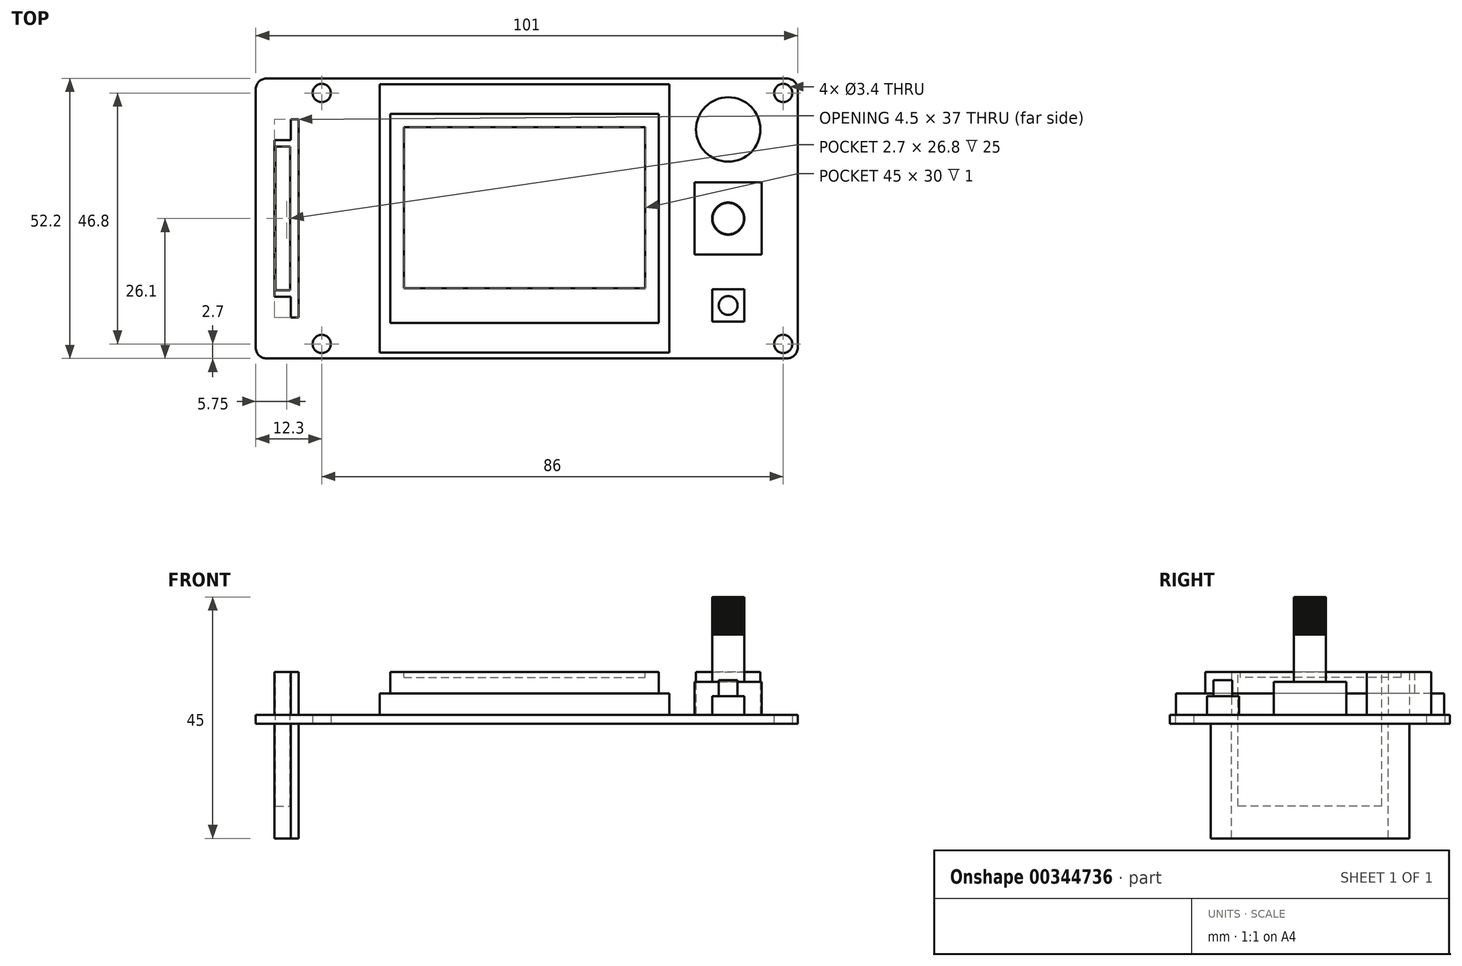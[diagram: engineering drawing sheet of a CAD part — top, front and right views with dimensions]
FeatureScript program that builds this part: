
annotation { "Feature Type Name" : "Feature", "Feature Type Description" : "" }
export const myFeature = defineFeature(function(context is Context, id is Id, definition is map)
    precondition{}
    {
        {
            var Q0;
            Q0=qCreatedBy(makeId("Top.planeOp"),FACE);
            var sketch = newSketch(context, id + "F0", { "sketchPlane" : qUnion([Q0])});
            skLineSegment(sketch, "E0.bottom", {"start": v(2, 0) * mm, "end": v(99, 0) * mm});
            skLineSegment(sketch, "E0.top", {"start": v(2, 52.2) * mm, "end": v(99, 52.2) * mm});
            skLineSegment(sketch, "E0.left", {"start": v(0, 2) * mm, "end": v(0, 50.2) * mm});
            skLineSegment(sketch, "E0.right", {"start": v(101, 2) * mm, "end": v(101, 50.2) * mm});
            skPoint(sketch, "E1.visualSharp", {"position": v(0, 52.2) * mm});
            skArc(sketch, "E1.filletArc", {"start": v(2, 52.2) * mm, "mid": v(0.59, 51.61) * mm, "end": v(0, 50.2) * mm});
            skPoint(sketch, "E2.visualSharp", {"position": v(101, 52.2) * mm});
            skArc(sketch, "E2.filletArc", {"start": v(101, 50.2) * mm, "mid": v(100.41, 51.61) * mm, "end": v(99, 52.2) * mm});
            skPoint(sketch, "E3.visualSharp", {"position": v(101, 0) * mm});
            skArc(sketch, "E3.filletArc", {"start": v(99, 0) * mm, "mid": v(100.41, 0.59) * mm, "end": v(101, 2) * mm});
            skPoint(sketch, "E4.visualSharp", {"position": v(0, 0) * mm});
            skArc(sketch, "E4.filletArc", {"start": v(0, 2) * mm, "mid": v(0.59, 0.59) * mm, "end": v(2, 0) * mm});
            skCircle(sketch, "E5", {"center": v(12.3, 49.5) * mm, "radius": 1.7 * mm});
            skCircle(sketch, "E6", {"center": v(98.3, 49.5) * mm, "radius": 1.7 * mm});
            skCircle(sketch, "E7", {"center": v(98.3, 2.7) * mm, "radius": 1.7 * mm});
            skCircle(sketch, "E8", {"center": v(12.3, 2.7) * mm, "radius": 1.7 * mm});
            skLineSegment(sketch, "E9", {"start": v(12.3, 49.5) * mm, "end": v(98.3, 49.5) * mm, "construction": true});
            skLineSegment(sketch, "E10", {"start": v(98.3, 2.7) * mm, "end": v(98.3, 49.5) * mm, "construction": true});
            skLineSegment(sketch, "E11", {"start": v(12.3, 2.7) * mm, "end": v(12.3, 49.5) * mm, "construction": true});
            skLineSegment(sketch, "E12", {"start": v(12.3, 2.7) * mm, "end": v(98.3, 2.7) * mm, "construction": true});
            skLineSegment(sketch, "E13", {"start": v(0, 26.1) * mm, "end": v(12.3, 26.1) * mm, "construction": true});
            skLineSegment(sketch, "E14", {"start": v(98.3, 26.1) * mm, "end": v(101, 26.1) * mm, "construction": true});
            skSolve(sketch);
        }
        {
            var Q0;
            Q0 = qSketchRegion(id + "F0", true);
            extrude(context, id + "F1", {"entities" : qUnion([Q0]), "depth" : 1.6 * mm});
        }
        {
            var Q0;
            Q0=makeQuery(id+"F1.opExtrude","CAP_FACE",FACE,{"disambiguationData":[OSD([sQuery(id+"F0.wireOp",EDGE,"E0.bottom"),sQuery(id+"F0.wireOp",EDGE,"E0.top"),sQuery(id+"F0.wireOp",EDGE,"E0.left"),sQuery(id+"F0.wireOp",EDGE,"E0.right"),sQuery(id+"F0.wireOp",EDGE,"E1.filletArc"),sQuery(id+"F0.wireOp",EDGE,"E2.filletArc"),sQuery(id+"F0.wireOp",EDGE,"E3.filletArc"),sQuery(id+"F0.wireOp",EDGE,"E4.filletArc"),sQuery(id+"F0.wireOp",EDGE,"E5"),sQuery(id+"F0.wireOp",EDGE,"E6"),sQuery(id+"F0.wireOp",EDGE,"E7"),sQuery(id+"F0.wireOp",EDGE,"E8")])],"isStart":false});
            var sketch = newSketch(context, id + "F2", { "sketchPlane" : qUnion([Q0])});
            skLineSegment(sketch, "E15.bottom", {"start": v(23.1, 51.1) * mm, "end": v(77.1, 51.1) * mm});
            skLineSegment(sketch, "E15.top", {"start": v(23.1, 1.1) * mm, "end": v(77.1, 1.1) * mm});
            skLineSegment(sketch, "E15.left", {"start": v(23.1, 51.1) * mm, "end": v(23.1, 1.1) * mm});
            skLineSegment(sketch, "E15.right", {"start": v(77.1, 51.1) * mm, "end": v(77.1, 1.1) * mm});
            skSolve(sketch);
        }
        {
            var Q0;
            Q0 = qSketchRegion(id + "F2", true);
            extrude(context, id + "F3", {"entities" : qUnion([Q0]), "operationType" : NewBodyOperationType.ADD, "depth" : 4 * mm});
        }
        {
            var Q0;
            Q0=makeQuery(id+"F3.opExtrude","CAP_FACE",FACE,{"disambiguationData":[OSD([sQuery(id+"F2.wireOp",EDGE,"E15.bottom"),sQuery(id+"F2.wireOp",EDGE,"E15.top"),sQuery(id+"F2.wireOp",EDGE,"E15.left"),sQuery(id+"F2.wireOp",EDGE,"E15.right")])],"isStart":false});
            var sketch = newSketch(context, id + "F4", { "sketchPlane" : qUnion([Q0])});
            skLineSegment(sketch, "E16", {"start": v(25.1, 45.6) * mm, "end": v(75.1, 45.6) * mm});
            skLineSegment(sketch, "E17", {"start": v(50.1, 51.1) * mm, "end": v(50.1, 45.6) * mm, "construction": true});
            skLineSegment(sketch, "E18", {"start": v(25.1, 45.6) * mm, "end": v(25.1, 6.6) * mm});
            skLineSegment(sketch, "E19", {"start": v(25.1, 6.6) * mm, "end": v(75.1, 6.6) * mm});
            skLineSegment(sketch, "E20", {"start": v(75.1, 6.6) * mm, "end": v(75.1, 45.6) * mm});
            skSolve(sketch);
        }
        {
            var Q0;
            Q0 = qSketchRegion(id + "F4", true);
            extrude(context, id + "F5", {"entities" : qUnion([Q0]), "operationType" : NewBodyOperationType.ADD, "depth" : 4 * mm});
        }
        {
            var Q0;
            Q0=makeQuery(id+"F1.opExtrude","CAP_FACE",FACE,{"disambiguationData":[OSD([sQuery(id+"F0.wireOp",EDGE,"E0.bottom"),sQuery(id+"F0.wireOp",EDGE,"E0.top"),sQuery(id+"F0.wireOp",EDGE,"E0.left"),sQuery(id+"F0.wireOp",EDGE,"E0.right"),sQuery(id+"F0.wireOp",EDGE,"E1.filletArc"),sQuery(id+"F0.wireOp",EDGE,"E2.filletArc"),sQuery(id+"F0.wireOp",EDGE,"E3.filletArc"),sQuery(id+"F0.wireOp",EDGE,"E4.filletArc"),sQuery(id+"F0.wireOp",EDGE,"E5"),sQuery(id+"F0.wireOp",EDGE,"E6"),sQuery(id+"F0.wireOp",EDGE,"E7"),sQuery(id+"F0.wireOp",EDGE,"E8")])],"isStart":false});
            var sketch = newSketch(context, id + "F6", { "sketchPlane" : qUnion([Q0])});
            skLineSegment(sketch, "E21", {"start": v(8, 44.6) * mm, "end": v(8, 7.6) * mm});
            skLineSegment(sketch, "E22", {"start": v(8, 7.6) * mm, "end": v(6.5, 7.6) * mm});
            skLineSegment(sketch, "E23", {"start": v(6.5, 7.6) * mm, "end": v(6.5, 11.5) * mm});
            skLineSegment(sketch, "E24", {"start": v(6.5, 11.5) * mm, "end": v(3.5, 11.5) * mm});
            skLineSegment(sketch, "E25", {"start": v(3.5, 11.5) * mm, "end": v(3.5, 40.7) * mm});
            skLineSegment(sketch, "E26", {"start": v(3.5, 40.7) * mm, "end": v(6.5, 40.7) * mm});
            skLineSegment(sketch, "E27", {"start": v(6.5, 40.7) * mm, "end": v(6.5, 44.6) * mm});
            skLineSegment(sketch, "E28", {"start": v(6.5, 44.6) * mm, "end": v(8, 44.6) * mm});
            skLineSegment(sketch, "E29", {"start": v(3.5, 26.1) * mm, "end": v(8, 26.1) * mm, "construction": true});
            skSolve(sketch);
        }
        {
            var Q0;
            Q0 = qSketchRegion(id + "F6", true);
            extrude(context, id + "F7", {"entities" : qUnion([Q0]), "operationType" : NewBodyOperationType.ADD, "depth" : 8 * mm});
        }
        {
            var Q0;
            Q0 = qSketchRegion(id + "F6", true);
            extrude(context, id + "F8", {"entities" : qUnion([Q0]), "operationType" : NewBodyOperationType.ADD, "oppositeDirection" : true, "depth" : 23 * mm});
        }
        {
            var Q0;
            Q0=makeQuery(id+"F7.opExtrude","CAP_FACE",FACE,{"disambiguationData":[OSD([sQuery(id+"F6.wireOp",EDGE,"E21"),sQuery(id+"F6.wireOp",EDGE,"E22"),sQuery(id+"F6.wireOp",EDGE,"E23"),sQuery(id+"F6.wireOp",EDGE,"E24"),sQuery(id+"F6.wireOp",EDGE,"E25"),sQuery(id+"F6.wireOp",EDGE,"E26"),sQuery(id+"F6.wireOp",EDGE,"E27"),sQuery(id+"F6.wireOp",EDGE,"E28")])],"isStart":false});
            var sketch = newSketch(context, id + "F9", { "sketchPlane" : qUnion([Q0])});
            skLineSegment(sketch, "E30.bottom", {"start": v(3.7, 39.5) * mm, "end": v(6.4, 39.5) * mm});
            skLineSegment(sketch, "E30.top", {"start": v(3.7, 12.7) * mm, "end": v(6.4, 12.7) * mm});
            skLineSegment(sketch, "E30.left", {"start": v(3.7, 39.5) * mm, "end": v(3.7, 12.7) * mm});
            skLineSegment(sketch, "E30.right", {"start": v(6.4, 39.5) * mm, "end": v(6.4, 12.7) * mm});
            skSolve(sketch);
        }
        {
            var Q0;
            Q0 = qSketchRegion(id + "F9", true);
            extrude(context, id + "F10", {"entities" : qUnion([Q0]), "operationType" : NewBodyOperationType.REMOVE, "oppositeDirection" : true, "depth" : 25 * mm});
        }
        {
            var Q0;
            Q0=makeQuery(id+"F1.opExtrude","CAP_FACE",FACE,{"disambiguationData":[OSD([sQuery(id+"F0.wireOp",EDGE,"E0.bottom"),sQuery(id+"F0.wireOp",EDGE,"E0.top"),sQuery(id+"F0.wireOp",EDGE,"E0.left"),sQuery(id+"F0.wireOp",EDGE,"E0.right"),sQuery(id+"F0.wireOp",EDGE,"E1.filletArc"),sQuery(id+"F0.wireOp",EDGE,"E2.filletArc"),sQuery(id+"F0.wireOp",EDGE,"E3.filletArc"),sQuery(id+"F0.wireOp",EDGE,"E4.filletArc"),sQuery(id+"F0.wireOp",EDGE,"E5"),sQuery(id+"F0.wireOp",EDGE,"E6"),sQuery(id+"F0.wireOp",EDGE,"E7"),sQuery(id+"F0.wireOp",EDGE,"E8")])],"isStart":false});
            var sketch = newSketch(context, id + "F11", { "sketchPlane" : qUnion([Q0])});
            skLineSegment(sketch, "E31.bottom", {"start": v(81.8, 32.85) * mm, "end": v(94.3, 32.85) * mm});
            skLineSegment(sketch, "E31.top", {"start": v(81.8, 19.35) * mm, "end": v(94.3, 19.35) * mm});
            skLineSegment(sketch, "E31.left", {"start": v(81.8, 32.85) * mm, "end": v(81.8, 19.35) * mm});
            skLineSegment(sketch, "E31.right", {"start": v(94.3, 32.85) * mm, "end": v(94.3, 19.35) * mm});
            skLineSegment(sketch, "E32", {"start": v(88.05, 32.85) * mm, "end": v(88.05, 19.35) * mm, "construction": true});
            skSolve(sketch);
        }
        {
            var Q0;
            Q0=makeQuery(id+"F1.opExtrude","CAP_FACE",FACE,{"disambiguationData":[OSD([sQuery(id+"F0.wireOp",EDGE,"E0.bottom"),sQuery(id+"F0.wireOp",EDGE,"E0.top"),sQuery(id+"F0.wireOp",EDGE,"E0.left"),sQuery(id+"F0.wireOp",EDGE,"E0.right"),sQuery(id+"F0.wireOp",EDGE,"E1.filletArc"),sQuery(id+"F0.wireOp",EDGE,"E2.filletArc"),sQuery(id+"F0.wireOp",EDGE,"E3.filletArc"),sQuery(id+"F0.wireOp",EDGE,"E4.filletArc"),sQuery(id+"F0.wireOp",EDGE,"E5"),sQuery(id+"F0.wireOp",EDGE,"E6"),sQuery(id+"F0.wireOp",EDGE,"E7"),sQuery(id+"F0.wireOp",EDGE,"E8")])],"isStart":false});
            var sketch = newSketch(context, id + "F12", { "sketchPlane" : qUnion([Q0])});
            skLineSegment(sketch, "E33", {"start": v(88.05, 36.7) * mm, "end": v(88.05, 52.2) * mm, "construction": true});
            skCircle(sketch, "E34", {"center": v(88.05, 42.7) * mm, "radius": 6 * mm});
            skLineSegment(sketch, "E35", {"start": v(88.05, 42.7) * mm, "end": v(94.05, 42.7) * mm, "construction": true});
            skSolve(sketch);
        }
        {
            var Q0;
            Q0 = qSketchRegion(id + "F12", true);
            extrude(context, id + "F13", {"entities" : qUnion([Q0]), "operationType" : NewBodyOperationType.ADD, "depth" : 8 * mm});
        }
        {
            var Q0;
            Q0=makeQuery(id+"F1.opExtrude","CAP_FACE",FACE,{"disambiguationData":[OSD([sQuery(id+"F0.wireOp",EDGE,"E0.bottom"),sQuery(id+"F0.wireOp",EDGE,"E0.top"),sQuery(id+"F0.wireOp",EDGE,"E0.left"),sQuery(id+"F0.wireOp",EDGE,"E0.right"),sQuery(id+"F0.wireOp",EDGE,"E1.filletArc"),sQuery(id+"F0.wireOp",EDGE,"E2.filletArc"),sQuery(id+"F0.wireOp",EDGE,"E3.filletArc"),sQuery(id+"F0.wireOp",EDGE,"E4.filletArc"),sQuery(id+"F0.wireOp",EDGE,"E5"),sQuery(id+"F0.wireOp",EDGE,"E6"),sQuery(id+"F0.wireOp",EDGE,"E7"),sQuery(id+"F0.wireOp",EDGE,"E8")])],"isStart":false});
            var sketch = newSketch(context, id + "F14", { "sketchPlane" : qUnion([Q0])});
            skLineSegment(sketch, "E36", {"start": v(85.05, 26.08) * mm, "end": v(91.05, 26.08) * mm, "construction": true});
            skLineSegment(sketch, "E37", {"start": v(88.05, 26.08) * mm, "end": v(88.05, 36.7) * mm, "construction": true});
            skCircle(sketch, "E38", {"center": v(88.05, 26.08) * mm, "radius": 3 * mm});
            skSolve(sketch);
        }
        {
            var Q0;
            Q0 = qSketchRegion(id + "F14", true);
            extrude(context, id + "F15", {"entities" : qUnion([Q0]), "operationType" : NewBodyOperationType.ADD, "depth" : 22 * mm});
        }
        {
            var Q0;
            Q0 = qSketchRegion(id + "F11", true);
            extrude(context, id + "F16", {"entities" : qUnion([Q0]), "operationType" : NewBodyOperationType.ADD, "depth" : 6.2 * mm});
        }
        {
            var Q0;
            Q0=makeQuery(id+"F15.opExtrude","CAP_FACE",FACE,{"disambiguationData":[OSD([sQuery(id+"F14.wireOp",EDGE,"E38")])],"isStart":false});
            var sketch = newSketch(context, id + "F17", { "sketchPlane" : qUnion([Q0])});
            skLineSegment(sketch, "E39", {"start": v(88.05, 26.08) * mm, "end": v(88.05, 29.08) * mm, "construction": true});
            skLineSegment(sketch, "E40", {"start": v(88.05, 29.08) * mm, "end": v(88.17, 28.87) * mm});
            skLineSegment(sketch, "E41", {"start": v(88.17, 28.87) * mm, "end": v(88.31, 29.06) * mm});
            skLineSegment(sketch, "E42", {"start": v(88.31, 29.06) * mm, "end": v(88.05, 26.08) * mm, "construction": true});
            skLineSegment(sketch, "E43", {"start": v(88.05, 29.08) * mm, "end": v(88.05, 30.08) * mm, "construction": true});
            skLineSegment(sketch, "E44", {"start": v(88.05, 30.08) * mm, "end": v(88.4, 30.06) * mm});
            skLineSegment(sketch, "E45", {"start": v(88.4, 30.06) * mm, "end": v(88.31, 29.06) * mm, "construction": true});
            skLineSegment(sketch, "E46.1.0", {"start": v(87.7, 30.06) * mm, "end": v(88.05, 30.08) * mm});
            skLineSegment(sketch, "E46.1.1", {"start": v(87.93, 28.87) * mm, "end": v(88.05, 29.08) * mm});
            skLineSegment(sketch, "E46.1.2", {"start": v(87.79, 29.06) * mm, "end": v(87.93, 28.87) * mm});
            skLineSegment(sketch, "E46.2.0", {"start": v(87.36, 30.01) * mm, "end": v(87.7, 30.06) * mm});
            skLineSegment(sketch, "E46.2.1", {"start": v(87.68, 28.85) * mm, "end": v(87.79, 29.06) * mm});
            skLineSegment(sketch, "E46.2.2", {"start": v(87.53, 29.03) * mm, "end": v(87.68, 28.85) * mm});
            skLineSegment(sketch, "E46.3.0", {"start": v(87.01, 29.94) * mm, "end": v(87.36, 30.01) * mm});
            skLineSegment(sketch, "E46.3.1", {"start": v(87.44, 28.8) * mm, "end": v(87.53, 29.03) * mm});
            skLineSegment(sketch, "E46.3.2", {"start": v(87.27, 28.97) * mm, "end": v(87.44, 28.8) * mm});
            skLineSegment(sketch, "E46.4.0", {"start": v(86.68, 29.83) * mm, "end": v(87.01, 29.94) * mm});
            skLineSegment(sketch, "E46.4.1", {"start": v(87.2, 28.75) * mm, "end": v(87.27, 28.97) * mm});
            skLineSegment(sketch, "E46.4.2", {"start": v(87.02, 28.9) * mm, "end": v(87.2, 28.75) * mm});
            skLineSegment(sketch, "E46.5.0", {"start": v(86.36, 29.7) * mm, "end": v(86.68, 29.83) * mm});
            skLineSegment(sketch, "E46.5.1", {"start": v(86.98, 28.66) * mm, "end": v(87.02, 28.9) * mm});
            skLineSegment(sketch, "E46.5.2", {"start": v(86.78, 28.8) * mm, "end": v(86.98, 28.66) * mm});
            skLineSegment(sketch, "E46.6.0", {"start": v(86.05, 29.54) * mm, "end": v(86.36, 29.7) * mm});
            skLineSegment(sketch, "E46.6.1", {"start": v(86.76, 28.56) * mm, "end": v(86.78, 28.8) * mm});
            skLineSegment(sketch, "E46.6.2", {"start": v(86.55, 28.67) * mm, "end": v(86.76, 28.56) * mm});
            skLineSegment(sketch, "E46.7.0", {"start": v(85.76, 29.35) * mm, "end": v(86.05, 29.54) * mm});
            skLineSegment(sketch, "E46.7.1", {"start": v(86.55, 28.44) * mm, "end": v(86.55, 28.67) * mm});
            skLineSegment(sketch, "E46.7.2", {"start": v(86.33, 28.53) * mm, "end": v(86.55, 28.44) * mm});
            skLineSegment(sketch, "E46.8.0", {"start": v(85.48, 29.14) * mm, "end": v(85.76, 29.35) * mm});
            skLineSegment(sketch, "E46.8.1", {"start": v(86.35, 28.3) * mm, "end": v(86.33, 28.53) * mm});
            skLineSegment(sketch, "E46.8.2", {"start": v(86.12, 28.37) * mm, "end": v(86.35, 28.3) * mm});
            skLineSegment(sketch, "E46.9.0", {"start": v(85.22, 28.9) * mm, "end": v(85.48, 29.14) * mm});
            skLineSegment(sketch, "E46.9.1", {"start": v(86.16, 28.14) * mm, "end": v(86.12, 28.37) * mm});
            skLineSegment(sketch, "E46.9.2", {"start": v(85.93, 28.2) * mm, "end": v(86.16, 28.14) * mm});
            skLineSegment(sketch, "E46.10.0", {"start": v(84.99, 28.65) * mm, "end": v(85.22, 28.9) * mm});
            skLineSegment(sketch, "E46.10.1", {"start": v(85.99, 27.97) * mm, "end": v(85.93, 28.2) * mm});
            skLineSegment(sketch, "E46.10.2", {"start": v(85.75, 28) * mm, "end": v(85.99, 27.97) * mm});
            skLineSegment(sketch, "E46.11.0", {"start": v(84.77, 28.37) * mm, "end": v(84.99, 28.65) * mm});
            skLineSegment(sketch, "E46.11.1", {"start": v(85.83, 27.78) * mm, "end": v(85.75, 28) * mm});
            skLineSegment(sketch, "E46.11.2", {"start": v(85.6, 27.8) * mm, "end": v(85.83, 27.78) * mm});
            skLineSegment(sketch, "E46.12.0", {"start": v(84.59, 28.07) * mm, "end": v(84.77, 28.37) * mm});
            skLineSegment(sketch, "E46.12.1", {"start": v(85.69, 27.58) * mm, "end": v(85.6, 27.8) * mm});
            skLineSegment(sketch, "E46.12.2", {"start": v(85.45, 27.58) * mm, "end": v(85.69, 27.58) * mm});
            skLineSegment(sketch, "E46.13.0", {"start": v(84.42, 27.77) * mm, "end": v(84.59, 28.07) * mm});
            skLineSegment(sketch, "E46.13.1", {"start": v(85.57, 27.37) * mm, "end": v(85.45, 27.57) * mm});
            skLineSegment(sketch, "E46.13.2", {"start": v(85.33, 27.34) * mm, "end": v(85.57, 27.37) * mm});
            skLineSegment(sketch, "E46.14.0", {"start": v(84.3, 27.44) * mm, "end": v(84.42, 27.77) * mm});
            skLineSegment(sketch, "E46.14.1", {"start": v(85.46, 27.15) * mm, "end": v(85.33, 27.34) * mm});
            skLineSegment(sketch, "E46.14.2", {"start": v(85.23, 27.1) * mm, "end": v(85.46, 27.15) * mm});
            skLineSegment(sketch, "E46.15.0", {"start": v(84.19, 27.11) * mm, "end": v(84.3, 27.44) * mm});
            skLineSegment(sketch, "E46.15.1", {"start": v(85.38, 26.92) * mm, "end": v(85.23, 27.1) * mm});
            skLineSegment(sketch, "E46.15.2", {"start": v(85.15, 26.85) * mm, "end": v(85.38, 26.92) * mm});
            skLineSegment(sketch, "E46.16.0", {"start": v(84.11, 26.77) * mm, "end": v(84.19, 27.11) * mm});
            skLineSegment(sketch, "E46.16.1", {"start": v(85.32, 26.68) * mm, "end": v(85.15, 26.85) * mm});
            skLineSegment(sketch, "E46.16.2", {"start": v(85.1, 26.6) * mm, "end": v(85.32, 26.68) * mm});
            skLineSegment(sketch, "E46.17.0", {"start": v(84.07, 26.42) * mm, "end": v(84.11, 26.77) * mm});
            skLineSegment(sketch, "E46.17.1", {"start": v(85.27, 26.44) * mm, "end": v(85.1, 26.6) * mm});
            skLineSegment(sketch, "E46.17.2", {"start": v(85.06, 26.34) * mm, "end": v(85.27, 26.44) * mm});
            skLineSegment(sketch, "E46.18.0", {"start": v(84.05, 26.07) * mm, "end": v(84.07, 26.42) * mm});
            skLineSegment(sketch, "E46.18.1", {"start": v(85.25, 26.2) * mm, "end": v(85.06, 26.34) * mm});
            skLineSegment(sketch, "E46.18.2", {"start": v(85.05, 26.08) * mm, "end": v(85.25, 26.2) * mm});
            skLineSegment(sketch, "E46.19.0", {"start": v(84.07, 25.73) * mm, "end": v(84.05, 26.07) * mm});
            skLineSegment(sketch, "E46.19.1", {"start": v(85.25, 25.95) * mm, "end": v(85.05, 26.07) * mm});
            skLineSegment(sketch, "E46.19.2", {"start": v(85.06, 25.81) * mm, "end": v(85.25, 25.95) * mm});
            skLineSegment(sketch, "E46.20.0", {"start": v(84.11, 25.38) * mm, "end": v(84.07, 25.73) * mm});
            skLineSegment(sketch, "E46.20.1", {"start": v(85.27, 25.7) * mm, "end": v(85.06, 25.81) * mm});
            skLineSegment(sketch, "E46.20.2", {"start": v(85.1, 25.55) * mm, "end": v(85.27, 25.7) * mm});
            skLineSegment(sketch, "E46.21.0", {"start": v(84.19, 25.04) * mm, "end": v(84.11, 25.38) * mm});
            skLineSegment(sketch, "E46.21.1", {"start": v(85.32, 25.47) * mm, "end": v(85.1, 25.55) * mm});
            skLineSegment(sketch, "E46.21.2", {"start": v(85.15, 25.3) * mm, "end": v(85.32, 25.47) * mm});
            skLineSegment(sketch, "E46.22.0", {"start": v(84.3, 24.7) * mm, "end": v(84.19, 25.04) * mm});
            skLineSegment(sketch, "E46.22.1", {"start": v(85.38, 25.23) * mm, "end": v(85.15, 25.3) * mm});
            skLineSegment(sketch, "E46.22.2", {"start": v(85.23, 25.05) * mm, "end": v(85.38, 25.23) * mm});
            skLineSegment(sketch, "E46.23.0", {"start": v(84.42, 24.38) * mm, "end": v(84.3, 24.7) * mm});
            skLineSegment(sketch, "E46.23.1", {"start": v(85.46, 25) * mm, "end": v(85.23, 25.05) * mm});
            skLineSegment(sketch, "E46.23.2", {"start": v(85.33, 24.8) * mm, "end": v(85.46, 25) * mm});
            skLineSegment(sketch, "E46.24.0", {"start": v(84.59, 24.08) * mm, "end": v(84.42, 24.38) * mm});
            skLineSegment(sketch, "E46.24.1", {"start": v(85.57, 24.78) * mm, "end": v(85.33, 24.8) * mm});
            skLineSegment(sketch, "E46.24.2", {"start": v(85.45, 24.58) * mm, "end": v(85.57, 24.78) * mm});
            skLineSegment(sketch, "E46.25.0", {"start": v(84.77, 23.78) * mm, "end": v(84.59, 24.07) * mm});
            skLineSegment(sketch, "E46.25.1", {"start": v(85.69, 24.57) * mm, "end": v(85.45, 24.58) * mm});
            skLineSegment(sketch, "E46.25.2", {"start": v(85.6, 24.35) * mm, "end": v(85.69, 24.57) * mm});
            skLineSegment(sketch, "E46.26.0", {"start": v(84.99, 23.5) * mm, "end": v(84.77, 23.78) * mm});
            skLineSegment(sketch, "E46.26.1", {"start": v(85.83, 24.37) * mm, "end": v(85.6, 24.35) * mm});
            skLineSegment(sketch, "E46.26.2", {"start": v(85.75, 24.15) * mm, "end": v(85.83, 24.37) * mm});
            skLineSegment(sketch, "E46.27.0", {"start": v(85.22, 23.25) * mm, "end": v(84.99, 23.5) * mm});
            skLineSegment(sketch, "E46.27.1", {"start": v(85.99, 24.18) * mm, "end": v(85.75, 24.15) * mm});
            skLineSegment(sketch, "E46.27.2", {"start": v(85.93, 23.95) * mm, "end": v(85.99, 24.18) * mm});
            skLineSegment(sketch, "E46.28.0", {"start": v(85.48, 23.01) * mm, "end": v(85.22, 23.25) * mm});
            skLineSegment(sketch, "E46.28.1", {"start": v(86.16, 24.01) * mm, "end": v(85.93, 23.95) * mm});
            skLineSegment(sketch, "E46.28.2", {"start": v(86.12, 23.78) * mm, "end": v(86.16, 24.01) * mm});
            skLineSegment(sketch, "E46.29.0", {"start": v(85.76, 22.8) * mm, "end": v(85.48, 23.01) * mm});
            skLineSegment(sketch, "E46.29.1", {"start": v(86.35, 23.85) * mm, "end": v(86.12, 23.78) * mm});
            skLineSegment(sketch, "E46.29.2", {"start": v(86.33, 23.62) * mm, "end": v(86.35, 23.85) * mm});
            skLineSegment(sketch, "E46.30.0", {"start": v(86.05, 22.61) * mm, "end": v(85.76, 22.8) * mm});
            skLineSegment(sketch, "E46.30.1", {"start": v(86.55, 23.71) * mm, "end": v(86.33, 23.62) * mm});
            skLineSegment(sketch, "E46.30.2", {"start": v(86.55, 23.48) * mm, "end": v(86.55, 23.71) * mm});
            skLineSegment(sketch, "E46.31.0", {"start": v(86.36, 22.45) * mm, "end": v(86.05, 22.61) * mm});
            skLineSegment(sketch, "E46.31.1", {"start": v(86.76, 23.6) * mm, "end": v(86.55, 23.48) * mm});
            skLineSegment(sketch, "E46.31.2", {"start": v(86.78, 23.36) * mm, "end": v(86.76, 23.6) * mm});
            skLineSegment(sketch, "E46.32.0", {"start": v(86.68, 22.32) * mm, "end": v(86.36, 22.45) * mm});
            skLineSegment(sketch, "E46.32.1", {"start": v(86.98, 23.49) * mm, "end": v(86.78, 23.36) * mm});
            skLineSegment(sketch, "E46.32.2", {"start": v(87.02, 23.26) * mm, "end": v(86.98, 23.49) * mm});
            skLineSegment(sketch, "E46.33.0", {"start": v(87.01, 22.21) * mm, "end": v(86.68, 22.32) * mm});
            skLineSegment(sketch, "E46.33.1", {"start": v(87.2, 23.4) * mm, "end": v(87.02, 23.26) * mm});
            skLineSegment(sketch, "E46.33.2", {"start": v(87.27, 23.18) * mm, "end": v(87.2, 23.4) * mm});
            skLineSegment(sketch, "E46.34.0", {"start": v(87.36, 22.14) * mm, "end": v(87.01, 22.21) * mm});
            skLineSegment(sketch, "E46.34.1", {"start": v(87.44, 23.34) * mm, "end": v(87.27, 23.18) * mm});
            skLineSegment(sketch, "E46.34.2", {"start": v(87.53, 23.12) * mm, "end": v(87.44, 23.34) * mm});
            skLineSegment(sketch, "E46.35.0", {"start": v(87.7, 22.1) * mm, "end": v(87.36, 22.14) * mm});
            skLineSegment(sketch, "E46.35.1", {"start": v(87.68, 23.3) * mm, "end": v(87.53, 23.12) * mm});
            skLineSegment(sketch, "E46.35.2", {"start": v(87.79, 23.09) * mm, "end": v(87.68, 23.3) * mm});
            skLineSegment(sketch, "E46.36.0", {"start": v(88.05, 22.07) * mm, "end": v(87.7, 22.1) * mm});
            skLineSegment(sketch, "E46.36.1", {"start": v(87.93, 23.28) * mm, "end": v(87.79, 23.09) * mm});
            skLineSegment(sketch, "E46.36.2", {"start": v(88.05, 23.07) * mm, "end": v(87.93, 23.28) * mm});
            skLineSegment(sketch, "E46.37.0", {"start": v(88.4, 22.1) * mm, "end": v(88.05, 22.08) * mm});
            skLineSegment(sketch, "E46.37.1", {"start": v(88.17, 23.28) * mm, "end": v(88.05, 23.07) * mm});
            skLineSegment(sketch, "E46.37.2", {"start": v(88.31, 23.09) * mm, "end": v(88.17, 23.28) * mm});
            skLineSegment(sketch, "E46.38.0", {"start": v(88.74, 22.14) * mm, "end": v(88.4, 22.1) * mm});
            skLineSegment(sketch, "E46.38.1", {"start": v(88.42, 23.3) * mm, "end": v(88.31, 23.09) * mm});
            skLineSegment(sketch, "E46.38.2", {"start": v(88.57, 23.12) * mm, "end": v(88.42, 23.3) * mm});
            skLineSegment(sketch, "E46.39.0", {"start": v(89.09, 22.21) * mm, "end": v(88.74, 22.14) * mm});
            skLineSegment(sketch, "E46.39.1", {"start": v(88.66, 23.34) * mm, "end": v(88.57, 23.12) * mm});
            skLineSegment(sketch, "E46.39.2", {"start": v(88.83, 23.18) * mm, "end": v(88.66, 23.34) * mm});
            skLineSegment(sketch, "E46.40.0", {"start": v(89.42, 22.32) * mm, "end": v(89.09, 22.21) * mm});
            skLineSegment(sketch, "E46.40.1", {"start": v(88.9, 23.4) * mm, "end": v(88.83, 23.18) * mm});
            skLineSegment(sketch, "E46.40.2", {"start": v(89.08, 23.26) * mm, "end": v(88.9, 23.4) * mm});
            skLineSegment(sketch, "E46.41.0", {"start": v(89.74, 22.45) * mm, "end": v(89.42, 22.32) * mm});
            skLineSegment(sketch, "E46.41.1", {"start": v(89.12, 23.49) * mm, "end": v(89.08, 23.26) * mm});
            skLineSegment(sketch, "E46.41.2", {"start": v(89.32, 23.36) * mm, "end": v(89.12, 23.49) * mm});
            skLineSegment(sketch, "E46.42.0", {"start": v(90.05, 22.61) * mm, "end": v(89.74, 22.45) * mm});
            skLineSegment(sketch, "E46.42.1", {"start": v(89.34, 23.6) * mm, "end": v(89.32, 23.36) * mm});
            skLineSegment(sketch, "E46.42.2", {"start": v(89.55, 23.48) * mm, "end": v(89.34, 23.6) * mm});
            skLineSegment(sketch, "E46.43.0", {"start": v(90.34, 22.8) * mm, "end": v(90.05, 22.61) * mm});
            skLineSegment(sketch, "E46.43.1", {"start": v(89.55, 23.71) * mm, "end": v(89.55, 23.48) * mm});
            skLineSegment(sketch, "E46.43.2", {"start": v(89.77, 23.62) * mm, "end": v(89.55, 23.71) * mm});
            skLineSegment(sketch, "E46.44.0", {"start": v(90.62, 23.01) * mm, "end": v(90.34, 22.8) * mm});
            skLineSegment(sketch, "E46.44.1", {"start": v(89.75, 23.85) * mm, "end": v(89.77, 23.62) * mm});
            skLineSegment(sketch, "E46.44.2", {"start": v(89.98, 23.78) * mm, "end": v(89.75, 23.85) * mm});
            skLineSegment(sketch, "E46.45.0", {"start": v(90.88, 23.25) * mm, "end": v(90.62, 23.01) * mm});
            skLineSegment(sketch, "E46.45.1", {"start": v(89.94, 24.01) * mm, "end": v(89.98, 23.78) * mm});
            skLineSegment(sketch, "E46.45.2", {"start": v(90.17, 23.95) * mm, "end": v(89.94, 24.01) * mm});
            skLineSegment(sketch, "E46.46.0", {"start": v(91.11, 23.5) * mm, "end": v(90.88, 23.25) * mm});
            skLineSegment(sketch, "E46.46.1", {"start": v(90.11, 24.18) * mm, "end": v(90.17, 23.95) * mm});
            skLineSegment(sketch, "E46.46.2", {"start": v(90.35, 24.15) * mm, "end": v(90.11, 24.18) * mm});
            skLineSegment(sketch, "E46.47.0", {"start": v(91.33, 23.78) * mm, "end": v(91.11, 23.5) * mm});
            skLineSegment(sketch, "E46.47.1", {"start": v(90.27, 24.37) * mm, "end": v(90.35, 24.15) * mm});
            skLineSegment(sketch, "E46.47.2", {"start": v(90.5, 24.35) * mm, "end": v(90.27, 24.37) * mm});
            skLineSegment(sketch, "E46.48.0", {"start": v(91.51, 24.08) * mm, "end": v(91.33, 23.78) * mm});
            skLineSegment(sketch, "E46.48.1", {"start": v(90.41, 24.57) * mm, "end": v(90.5, 24.35) * mm});
            skLineSegment(sketch, "E46.48.2", {"start": v(90.65, 24.57) * mm, "end": v(90.41, 24.57) * mm});
            skLineSegment(sketch, "E46.49.0", {"start": v(91.68, 24.38) * mm, "end": v(91.51, 24.08) * mm});
            skLineSegment(sketch, "E46.49.1", {"start": v(90.53, 24.78) * mm, "end": v(90.65, 24.58) * mm});
            skLineSegment(sketch, "E46.49.2", {"start": v(90.77, 24.8) * mm, "end": v(90.53, 24.78) * mm});
            skLineSegment(sketch, "E46.50.0", {"start": v(91.8, 24.7) * mm, "end": v(91.68, 24.38) * mm});
            skLineSegment(sketch, "E46.50.1", {"start": v(90.64, 25) * mm, "end": v(90.77, 24.8) * mm});
            skLineSegment(sketch, "E46.50.2", {"start": v(90.87, 25.05) * mm, "end": v(90.64, 25) * mm});
            skLineSegment(sketch, "E46.51.0", {"start": v(91.91, 25.04) * mm, "end": v(91.8, 24.7) * mm});
            skLineSegment(sketch, "E46.51.1", {"start": v(90.72, 25.23) * mm, "end": v(90.87, 25.05) * mm});
            skLineSegment(sketch, "E46.51.2", {"start": v(90.95, 25.3) * mm, "end": v(90.72, 25.23) * mm});
            skLineSegment(sketch, "E46.52.0", {"start": v(91.99, 25.38) * mm, "end": v(91.91, 25.04) * mm});
            skLineSegment(sketch, "E46.52.1", {"start": v(90.78, 25.47) * mm, "end": v(90.95, 25.3) * mm});
            skLineSegment(sketch, "E46.52.2", {"start": v(91, 25.55) * mm, "end": v(90.78, 25.47) * mm});
            skLineSegment(sketch, "E46.53.0", {"start": v(92.03, 25.73) * mm, "end": v(91.99, 25.38) * mm});
            skLineSegment(sketch, "E46.53.1", {"start": v(90.83, 25.7) * mm, "end": v(91, 25.55) * mm});
            skLineSegment(sketch, "E46.53.2", {"start": v(91.04, 25.81) * mm, "end": v(90.83, 25.7) * mm});
            skLineSegment(sketch, "E46.54.0", {"start": v(92.05, 26.08) * mm, "end": v(92.03, 25.73) * mm});
            skLineSegment(sketch, "E46.54.1", {"start": v(90.85, 25.95) * mm, "end": v(91.04, 25.81) * mm});
            skLineSegment(sketch, "E46.54.2", {"start": v(91.05, 26.07) * mm, "end": v(90.85, 25.95) * mm});
            skLineSegment(sketch, "E46.55.0", {"start": v(92.03, 26.42) * mm, "end": v(92.05, 26.08) * mm});
            skLineSegment(sketch, "E46.55.1", {"start": v(90.85, 26.2) * mm, "end": v(91.05, 26.08) * mm});
            skLineSegment(sketch, "E46.55.2", {"start": v(91.04, 26.34) * mm, "end": v(90.85, 26.2) * mm});
            skLineSegment(sketch, "E46.56.0", {"start": v(91.99, 26.77) * mm, "end": v(92.03, 26.42) * mm});
            skLineSegment(sketch, "E46.56.1", {"start": v(90.83, 26.44) * mm, "end": v(91.04, 26.34) * mm});
            skLineSegment(sketch, "E46.56.2", {"start": v(91, 26.6) * mm, "end": v(90.83, 26.44) * mm});
            skLineSegment(sketch, "E46.57.0", {"start": v(91.91, 27.11) * mm, "end": v(91.99, 26.77) * mm});
            skLineSegment(sketch, "E46.57.1", {"start": v(90.78, 26.68) * mm, "end": v(91, 26.6) * mm});
            skLineSegment(sketch, "E46.57.2", {"start": v(90.95, 26.85) * mm, "end": v(90.78, 26.68) * mm});
            skLineSegment(sketch, "E46.58.0", {"start": v(91.8, 27.44) * mm, "end": v(91.91, 27.11) * mm});
            skLineSegment(sketch, "E46.58.1", {"start": v(90.72, 26.92) * mm, "end": v(90.95, 26.85) * mm});
            skLineSegment(sketch, "E46.58.2", {"start": v(90.87, 27.1) * mm, "end": v(90.72, 26.92) * mm});
            skLineSegment(sketch, "E46.59.0", {"start": v(91.68, 27.77) * mm, "end": v(91.8, 27.44) * mm});
            skLineSegment(sketch, "E46.59.1", {"start": v(90.64, 27.15) * mm, "end": v(90.87, 27.1) * mm});
            skLineSegment(sketch, "E46.59.2", {"start": v(90.77, 27.34) * mm, "end": v(90.64, 27.15) * mm});
            skLineSegment(sketch, "E46.60.0", {"start": v(91.51, 28.07) * mm, "end": v(91.68, 27.77) * mm});
            skLineSegment(sketch, "E46.60.1", {"start": v(90.53, 27.37) * mm, "end": v(90.77, 27.34) * mm});
            skLineSegment(sketch, "E46.60.2", {"start": v(90.65, 27.57) * mm, "end": v(90.53, 27.37) * mm});
            skLineSegment(sketch, "E46.61.0", {"start": v(91.33, 28.37) * mm, "end": v(91.51, 28.08) * mm});
            skLineSegment(sketch, "E46.61.1", {"start": v(90.41, 27.58) * mm, "end": v(90.65, 27.58) * mm});
            skLineSegment(sketch, "E46.61.2", {"start": v(90.5, 27.8) * mm, "end": v(90.41, 27.58) * mm});
            skLineSegment(sketch, "E46.62.0", {"start": v(91.11, 28.65) * mm, "end": v(91.33, 28.37) * mm});
            skLineSegment(sketch, "E46.62.1", {"start": v(90.27, 27.78) * mm, "end": v(90.5, 27.8) * mm});
            skLineSegment(sketch, "E46.62.2", {"start": v(90.35, 28) * mm, "end": v(90.27, 27.78) * mm});
            skLineSegment(sketch, "E46.63.0", {"start": v(90.88, 28.9) * mm, "end": v(91.11, 28.65) * mm});
            skLineSegment(sketch, "E46.63.1", {"start": v(90.11, 27.97) * mm, "end": v(90.35, 28) * mm});
            skLineSegment(sketch, "E46.63.2", {"start": v(90.17, 28.2) * mm, "end": v(90.11, 27.97) * mm});
            skLineSegment(sketch, "E46.64.0", {"start": v(90.62, 29.14) * mm, "end": v(90.88, 28.9) * mm});
            skLineSegment(sketch, "E46.64.1", {"start": v(89.94, 28.14) * mm, "end": v(90.17, 28.2) * mm});
            skLineSegment(sketch, "E46.64.2", {"start": v(89.98, 28.37) * mm, "end": v(89.94, 28.14) * mm});
            skLineSegment(sketch, "E46.65.0", {"start": v(90.34, 29.35) * mm, "end": v(90.62, 29.14) * mm});
            skLineSegment(sketch, "E46.65.1", {"start": v(89.75, 28.3) * mm, "end": v(89.98, 28.37) * mm});
            skLineSegment(sketch, "E46.65.2", {"start": v(89.77, 28.53) * mm, "end": v(89.75, 28.3) * mm});
            skLineSegment(sketch, "E46.66.0", {"start": v(90.05, 29.54) * mm, "end": v(90.34, 29.35) * mm});
            skLineSegment(sketch, "E46.66.1", {"start": v(89.55, 28.44) * mm, "end": v(89.77, 28.53) * mm});
            skLineSegment(sketch, "E46.66.2", {"start": v(89.55, 28.67) * mm, "end": v(89.55, 28.44) * mm});
            skLineSegment(sketch, "E46.67.0", {"start": v(89.74, 29.7) * mm, "end": v(90.05, 29.54) * mm});
            skLineSegment(sketch, "E46.67.1", {"start": v(89.34, 28.56) * mm, "end": v(89.55, 28.67) * mm});
            skLineSegment(sketch, "E46.67.2", {"start": v(89.32, 28.8) * mm, "end": v(89.34, 28.56) * mm});
            skLineSegment(sketch, "E46.68.0", {"start": v(89.42, 29.83) * mm, "end": v(89.74, 29.7) * mm});
            skLineSegment(sketch, "E46.68.1", {"start": v(89.12, 28.66) * mm, "end": v(89.32, 28.8) * mm});
            skLineSegment(sketch, "E46.68.2", {"start": v(89.08, 28.9) * mm, "end": v(89.12, 28.66) * mm});
            skLineSegment(sketch, "E46.69.0", {"start": v(89.09, 29.94) * mm, "end": v(89.42, 29.83) * mm});
            skLineSegment(sketch, "E46.69.1", {"start": v(88.9, 28.75) * mm, "end": v(89.08, 28.9) * mm});
            skLineSegment(sketch, "E46.69.2", {"start": v(88.83, 28.97) * mm, "end": v(88.9, 28.75) * mm});
            skLineSegment(sketch, "E46.70.0", {"start": v(88.74, 30.01) * mm, "end": v(89.09, 29.94) * mm});
            skLineSegment(sketch, "E46.70.1", {"start": v(88.66, 28.8) * mm, "end": v(88.83, 28.97) * mm});
            skLineSegment(sketch, "E46.70.2", {"start": v(88.57, 29.03) * mm, "end": v(88.66, 28.8) * mm});
            skLineSegment(sketch, "E46.71.0", {"start": v(88.4, 30.06) * mm, "end": v(88.74, 30.01) * mm});
            skLineSegment(sketch, "E46.71.1", {"start": v(88.42, 28.85) * mm, "end": v(88.57, 29.03) * mm});
            skLineSegment(sketch, "E46.71.2", {"start": v(88.31, 29.06) * mm, "end": v(88.42, 28.85) * mm});
            skPoint(sketch, "E46.center", {"position": v(88.05, 26.08) * mm});
            skSolve(sketch);
        }
        {
            var Q0;
            Q0 = qSketchRegion(id + "F17", true);
            extrude(context, id + "F18", {"entities" : qUnion([Q0]), "operationType" : NewBodyOperationType.REMOVE, "oppositeDirection" : true, "depth" : 7 * mm});
        }
        {
            var Q0;
            Q0=makeQuery(id+"F1.opExtrude","CAP_FACE",FACE,{"disambiguationData":[OSD([sQuery(id+"F0.wireOp",EDGE,"E0.bottom"),sQuery(id+"F0.wireOp",EDGE,"E0.top"),sQuery(id+"F0.wireOp",EDGE,"E0.left"),sQuery(id+"F0.wireOp",EDGE,"E0.right"),sQuery(id+"F0.wireOp",EDGE,"E1.filletArc"),sQuery(id+"F0.wireOp",EDGE,"E2.filletArc"),sQuery(id+"F0.wireOp",EDGE,"E3.filletArc"),sQuery(id+"F0.wireOp",EDGE,"E4.filletArc"),sQuery(id+"F0.wireOp",EDGE,"E5"),sQuery(id+"F0.wireOp",EDGE,"E6"),sQuery(id+"F0.wireOp",EDGE,"E7"),sQuery(id+"F0.wireOp",EDGE,"E8")])],"isStart":false});
            var sketch = newSketch(context, id + "F19", { "sketchPlane" : qUnion([Q0])});
            skLineSegment(sketch, "E47.bottom", {"start": v(85.05, 12.88) * mm, "end": v(91.05, 12.88) * mm});
            skLineSegment(sketch, "E47.top", {"start": v(85.05, 6.88) * mm, "end": v(91.05, 6.88) * mm});
            skLineSegment(sketch, "E47.left", {"start": v(85.05, 12.88) * mm, "end": v(85.05, 6.88) * mm});
            skLineSegment(sketch, "E47.right", {"start": v(91.05, 12.88) * mm, "end": v(91.05, 6.88) * mm});
            skLineSegment(sketch, "E48", {"start": v(88.05, 19.35) * mm, "end": v(88.05, 12.88) * mm, "construction": true});
            skSolve(sketch);
        }
        {
            var Q0;
            Q0 = qSketchRegion(id + "F19", true);
            extrude(context, id + "F20", {"entities" : qUnion([Q0]), "operationType" : NewBodyOperationType.ADD, "depth" : 3.5 * mm});
        }
        {
            var Q0;
            Q0=makeQuery(id+"F20.opExtrude","CAP_FACE",FACE,{"disambiguationData":[OSD([sQuery(id+"F19.wireOp",EDGE,"E47.bottom"),sQuery(id+"F19.wireOp",EDGE,"E47.top"),sQuery(id+"F19.wireOp",EDGE,"E47.left"),sQuery(id+"F19.wireOp",EDGE,"E47.right")])],"isStart":false});
            var sketch = newSketch(context, id + "F21", { "sketchPlane" : qUnion([Q0])});
            skCircle(sketch, "E49", {"center": v(88.05, 9.88) * mm, "radius": 1.75 * mm});
            skLineSegment(sketch, "E50", {"start": v(88.05, 9.88) * mm, "end": v(91.05, 9.88) * mm, "construction": true});
            skLineSegment(sketch, "E51", {"start": v(88.05, 9.88) * mm, "end": v(88.05, 6.88) * mm, "construction": true});
            skSolve(sketch);
        }
        {
            var Q0;
            Q0 = qSketchRegion(id + "F21", true);
            extrude(context, id + "F22", {"entities" : qUnion([Q0]), "operationType" : NewBodyOperationType.ADD, "depth" : 3 * mm});
        }
        {
            var Q0;
            Q0=makeQuery(id+"F5.opExtrude","CAP_FACE",FACE,{"disambiguationData":[OSD([sQuery(id+"F4.wireOp",EDGE,"E16"),sQuery(id+"F4.wireOp",EDGE,"E18"),sQuery(id+"F4.wireOp",EDGE,"E19"),sQuery(id+"F4.wireOp",EDGE,"E20")])],"isStart":false});
            var sketch = newSketch(context, id + "F23", { "sketchPlane" : qUnion([Q0])});
            skLineSegment(sketch, "E52.bottom", {"start": v(27.6, 43.1) * mm, "end": v(72.6, 43.1) * mm});
            skLineSegment(sketch, "E52.top", {"start": v(27.6, 13.1) * mm, "end": v(72.6, 13.1) * mm});
            skLineSegment(sketch, "E52.left", {"start": v(27.6, 43.1) * mm, "end": v(27.6, 13.1) * mm});
            skLineSegment(sketch, "E52.right", {"start": v(72.6, 43.1) * mm, "end": v(72.6, 13.1) * mm});
            skLineSegment(sketch, "E53", {"start": v(50.1, 43.1) * mm, "end": v(50.1, 45.6) * mm, "construction": true});
            skSolve(sketch);
        }
        {
            var Q0;
            Q0 = qSketchRegion(id + "F23", true);
            extrude(context, id + "F24", {"entities" : qUnion([Q0]), "operationType" : NewBodyOperationType.REMOVE, "oppositeDirection" : true, "depth" : 1 * mm});
        }
    });
